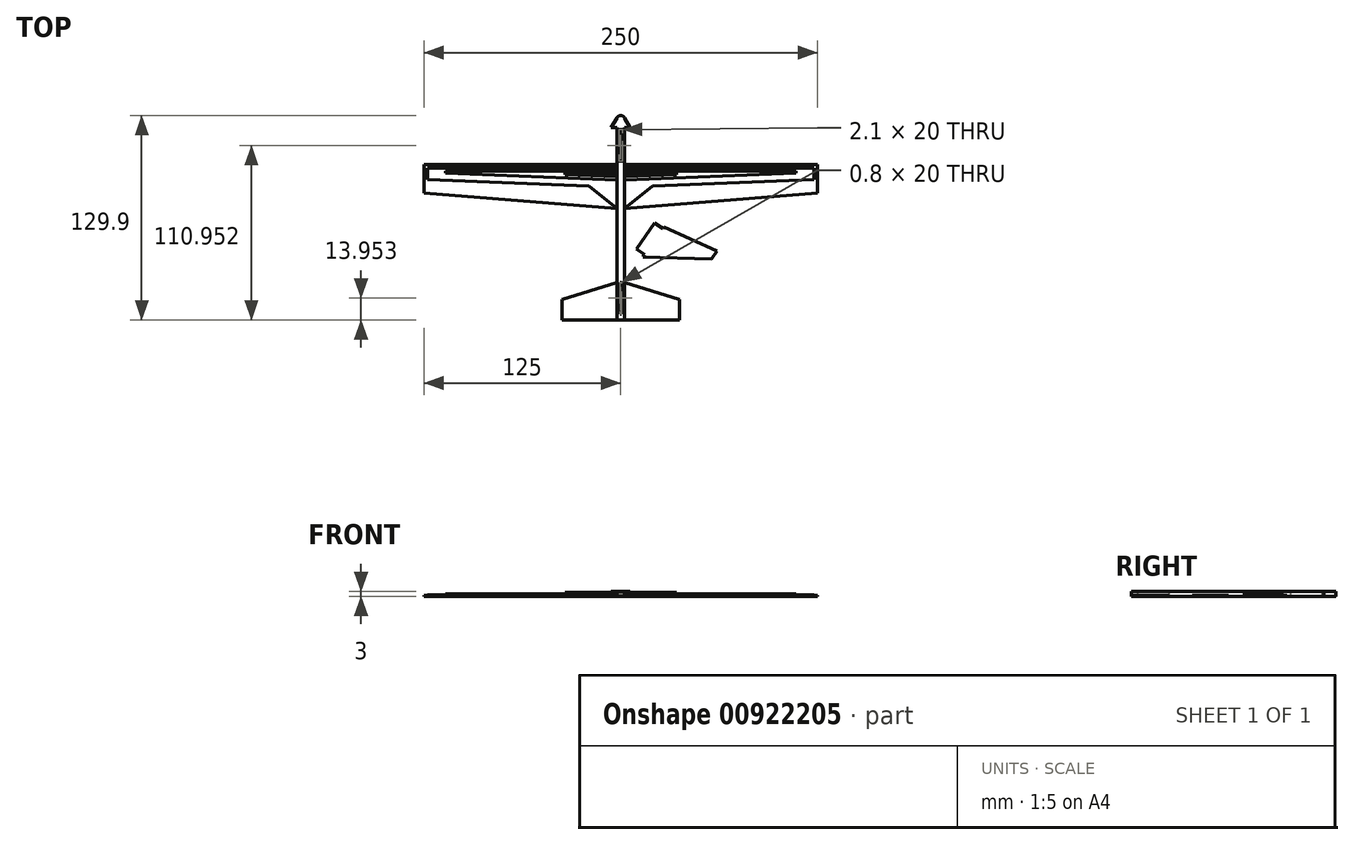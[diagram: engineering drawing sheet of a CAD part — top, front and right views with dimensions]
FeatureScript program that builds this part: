
annotation { "Feature Type Name" : "Feature", "Feature Type Description" : "" }
export const myFeature = defineFeature(function(context is Context, id is Id, definition is map)
    precondition{}
    {
        {
            var Q0;
            Q0=qCreatedBy(makeId("Top.planeOp"),FACE);
            var sketch = newSketch(context, id + "F0", { "sketchPlane" : qUnion([Q0])});
            skLineSegment(sketch, "E0", {"start": v(0, 139.35) * mm, "end": v(0, -90.2) * mm, "construction": true});
            skLineSegment(sketch, "E1", {"start": v(-125, 0) * mm, "end": v(0, 0) * mm, "construction": true});
            skLineSegment(sketch, "E2", {"start": v(0, 38.23) * mm, "end": v(-2.5, 38.23) * mm});
            skLineSegment(sketch, "E3", {"start": v(-2.5, 38.23) * mm, "end": v(-2.5, -90.2) * mm});
            skLineSegment(sketch, "E4", {"start": v(-2.5, -90.2) * mm, "end": v(0, -90.2) * mm});
            skLineSegment(sketch, "E5", {"start": v(-2.5, 8.48) * mm, "end": v(-125, 8.48) * mm});
            skLineSegment(sketch, "E6", {"start": v(-125, 8.48) * mm, "end": v(-125, 0) * mm});
            skLineSegment(sketch, "E7", {"start": v(-125, -9.54) * mm, "end": v(-2.5, -19.38) * mm});
            skLineSegment(sketch, "E8", {"start": v(-125, -9.54) * mm, "end": v(-125, 0) * mm});
            skLineSegment(sketch, "E9", {"start": v(-2.5, -66.26) * mm, "end": v(-37.22, -77.08) * mm});
            skLineSegment(sketch, "E10", {"start": v(-37.22, -77.08) * mm, "end": v(-37.22, -90.2) * mm});
            skLineSegment(sketch, "E11", {"start": v(-37.22, -90.2) * mm, "end": v(-2.5, -90.2) * mm});
            skLineSegment(sketch, "E12.MirrorCS", {"start": v(2.5, -90.2) * mm, "end": v(0, -90.2) * mm});
            skLineSegment(sketch, "E13.MirrorCS", {"start": v(37.22, -77.08) * mm, "end": v(37.22, -90.2) * mm});
            skLineSegment(sketch, "E14.MirrorCS", {"start": v(0, 38.23) * mm, "end": v(2.5, 38.23) * mm});
            skLineSegment(sketch, "E15.MirrorCS", {"start": v(37.22, -90.2) * mm, "end": v(2.5, -90.2) * mm});
            skLineSegment(sketch, "E16.MirrorCS", {"start": v(125, 0) * mm, "end": v(0, 0) * mm, "construction": true});
            skLineSegment(sketch, "E17.MirrorCS", {"start": v(2.5, 38.23) * mm, "end": v(2.5, -90.2) * mm});
            skLineSegment(sketch, "E18.MirrorCS", {"start": v(2.5, 8.48) * mm, "end": v(125, 8.48) * mm});
            skLineSegment(sketch, "E19.MirrorCS", {"start": v(125, 8.48) * mm, "end": v(125, 0) * mm});
            skLineSegment(sketch, "E20.MirrorCS", {"start": v(125, -9.54) * mm, "end": v(2.5, -19.38) * mm});
            skLineSegment(sketch, "E21.MirrorCS", {"start": v(2.5, -66.26) * mm, "end": v(37.22, -77.08) * mm});
            skLineSegment(sketch, "E22.MirrorCS", {"start": v(125, -9.54) * mm, "end": v(125, 0) * mm});
            skLineSegment(sketch, "E23", {"start": v(0, -66.26) * mm, "end": v(-0.4, -66.26) * mm});
            skLineSegment(sketch, "E24", {"start": v(-0.4, -66.26) * mm, "end": v(-0.4, -86.26) * mm});
            skLineSegment(sketch, "E25", {"start": v(-0.4, -86.26) * mm, "end": v(0, -86.26) * mm});
            skLineSegment(sketch, "E26.MirrorCS", {"start": v(0, -66.26) * mm, "end": v(0.4, -66.26) * mm});
            skLineSegment(sketch, "E27.MirrorCS", {"start": v(0.4, -66.26) * mm, "end": v(0.4, -86.26) * mm});
            skLineSegment(sketch, "E28.MirrorCS", {"start": v(0.4, -86.26) * mm, "end": v(0, -86.26) * mm});
            skLineSegment(sketch, "E29", {"start": v(14.14, -50.16) * mm, "end": v(57.48, -51.39) * mm});
            skLineSegment(sketch, "E30", {"start": v(57.48, -51.39) * mm, "end": v(61.1, -46.22) * mm});
            skLineSegment(sketch, "E31", {"start": v(61.1, -46.22) * mm, "end": v(27.57, -30.97) * mm});
            skLineSegment(sketch, "E32", {"start": v(27.57, -30.97) * mm, "end": v(26.7, -32.22) * mm});
            skLineSegment(sketch, "E33", {"start": v(26.7, -32.22) * mm, "end": v(21.46, -28.56) * mm});
            skLineSegment(sketch, "E34", {"start": v(9.98, -44.94) * mm, "end": v(15.22, -48.6) * mm});
            skLineSegment(sketch, "E35", {"start": v(15.22, -48.6) * mm, "end": v(14.14, -50.16) * mm});
            skLineSegment(sketch, "E36", {"start": v(9.98, -44.94) * mm, "end": v(21.46, -28.56) * mm});
            skLineSegment(sketch, "E37.0", {"start": v(27.57, -30.97) * mm, "end": v(14.14, -50.16) * mm, "construction": true});
            skLineSegment(sketch, "E38", {"start": v(0, 30.74) * mm, "end": v(-1.05, 30.74) * mm});
            skLineSegment(sketch, "E39", {"start": v(-1.05, 30.74) * mm, "end": v(-1.05, 10.74) * mm});
            skLineSegment(sketch, "E40", {"start": v(-1.05, 10.74) * mm, "end": v(0, 10.74) * mm});
            skLineSegment(sketch, "E41.MirrorCS", {"start": v(0, 30.74) * mm, "end": v(1.05, 30.74) * mm});
            skLineSegment(sketch, "E42.MirrorCS", {"start": v(1.05, 30.74) * mm, "end": v(1.05, 10.74) * mm});
            skLineSegment(sketch, "E43.MirrorCS", {"start": v(1.05, 10.74) * mm, "end": v(0, 10.74) * mm});
            skLineSegment(sketch, "E44", {"start": v(-2.5, 38.23) * mm, "end": v(-6.03, 31.96) * mm});
            skLineSegment(sketch, "E45", {"start": v(-6.03, 31.96) * mm, "end": v(-2.5, 31.96) * mm});
            skLineSegment(sketch, "E46.MirrorCS", {"start": v(2.5, 38.23) * mm, "end": v(6.03, 31.96) * mm});
            skLineSegment(sketch, "E47.MirrorCS", {"start": v(6.03, 31.96) * mm, "end": v(2.5, 31.96) * mm});
            skArc(sketch, "E48", {"start": v(2.5, 38.23) * mm, "mid": v(0, 39.69) * mm, "end": v(-2.5, 38.23) * mm});
            skSolve(sketch);
        }
        {
            var Q0;
            {var subQ1=sQuery(id+"F0.wireOp",EDGE,"E5");Q0=makeQuery(id+"F0.imprint","IMPRINT",FACE,{"disambiguationData":[TD([[makeQuery(id+"F0.imprint","IMPRINT",EDGE,{"derivedFrom":subQ1}),1.0]])]});}
            var Q1;
            {var subQ2=sQuery(id+"F0.wireOp",EDGE,"E9");Q1=makeQuery(id+"F0.imprint","IMPRINT",FACE,{"disambiguationData":[TD([[makeQuery(id+"F0.imprint","IMPRINT",EDGE,{"derivedFrom":subQ2}),1.0]])]});}
            var Q2;
            Q2=makeQuery(id+"F0.imprint","IMPRINT",FACE,{"disambiguationData":[TD([[makeQuery(id+"F0.imprint","IMPRINT",EDGE,{"derivedFrom":sQuery(id+"F0.wireOp",EDGE,"E13.MirrorCS")}),-1.0]])]});
            var Q3;
            {var subQ0=sQuery(id+"F0.wireOp",EDGE,"E18.MirrorCS");Q3=makeQuery(id+"F0.imprint","IMPRINT",FACE,{"disambiguationData":[TD([[makeQuery(id+"F0.imprint","IMPRINT",EDGE,{"derivedFrom":subQ0}),-1.0]])]});}
            var Q4;
            {var subQ7=sQuery(id+"F0.wireOp",EDGE,"E2");Q4=makeQuery(id+"F0.imprint","IMPRINT",FACE,{"disambiguationData":[TD([[makeQuery(id+"F0.imprint","IMPRINT",EDGE,{"derivedFrom":subQ7}),1.0]])]});}
            extrude(context, id + "F1", {"entities" : qUnion([Q0, Q1, Q2, Q3, Q4]), "depth" : 0.5 * mm, "offsetDistance" : 25 * mm});
        }
        {
            var Q0;
            {var subQ7=sQuery(id+"F0.wireOp",EDGE,"E2");Q0=makeQuery(id+"F0.imprint","IMPRINT",FACE,{"disambiguationData":[TD([[makeQuery(id+"F0.imprint","IMPRINT",EDGE,{"derivedFrom":subQ7}),1.0]])]});}
            var Q1;
            {var subQ0=sQuery(id+"F0.wireOp",EDGE,"fwCbbQgS-ba7Q-RRvG-tuf4-dKK3rzpyElhT");Q1=makeQuery(id+"F0.imprint","IMPRINT",FACE,{"disambiguationData":[TD([[makeQuery(id+"F0.imprint","IMPRINT",EDGE,{"derivedFrom":subQ0}),1.0]])]});}
            var Q2;
            {var subQ0=sQuery(id+"F0.wireOp",EDGE,"E44");Q2=makeQuery(id+"F0.imprint","IMPRINT",FACE,{"disambiguationData":[TD([[makeQuery(id+"F0.imprint","IMPRINT",EDGE,{"derivedFrom":subQ0}),1.0]])]});}
            var Q3;
            {var subQ0=sQuery(id+"F0.wireOp",EDGE,"E46.MirrorCS");Q3=makeQuery(id+"F0.imprint","IMPRINT",FACE,{"disambiguationData":[TD([[makeQuery(id+"F0.imprint","IMPRINT",EDGE,{"derivedFrom":subQ0}),-1.0]])]});}
            var Q4;
            Q4=makeQuery(id+"F0.imprint","IMPRINT",FACE,{"disambiguationData":[TD([[makeQuery(id+"F0.imprint","IMPRINT",EDGE,{"derivedFrom":sQuery(id+"F0.wireOp",EDGE,"E2")}),-1.0]])]});
            extrude(context, id + "F2", {"entities" : qUnion([Q0, Q1, Q2, Q3, Q4]), "operationType" : NewBodyOperationType.ADD, "depth" : 3 * mm, "offsetDistance" : 25 * mm});
        }
        {
            var Q0;
            {var subQ0=sQuery(id+"F0.wireOp",EDGE,"E8");var subQ1=sQuery(id+"F0.wireOp",EDGE,"E6");var subQ2=sQuery(id+"F0.wireOp",EDGE,"E3");var subQ3=sQuery(id+"F0.wireOp",EDGE,"E5");var subQ4=sQuery(id+"F0.wireOp",EDGE,"E7");var subQ5=sQuery(id+"F0.wireOp",EDGE,"E9");var subQ6=sQuery(id+"F0.wireOp",EDGE,"E2");Q0=makeQuery(id+"F2.boolean.opBoolean","SPLIT",FACE,{"disambiguationData":[TD([makeQuery(id+"F1.opExtrude","SWEPT_FACE",FACE,{"disambiguationData":[OSD([subQ3])]})])],"derivedFrom":makeQuery(id+"F1.opExtrude","CAP_FACE",FACE,{"disambiguationData":[OSD([subQ6,subQ2,sQuery(id+"F0.wireOp",EDGE,"E4"),subQ3,subQ1,subQ4,subQ0,subQ5,sQuery(id+"F0.wireOp",EDGE,"E10"),sQuery(id+"F0.wireOp",EDGE,"E11"),sQuery(id+"F0.wireOp",EDGE,"E12.MirrorCS"),sQuery(id+"F0.wireOp",EDGE,"E13.MirrorCS"),sQuery(id+"F0.wireOp",EDGE,"E14.MirrorCS"),sQuery(id+"F0.wireOp",EDGE,"E15.MirrorCS"),sQuery(id+"F0.wireOp",EDGE,"E17.MirrorCS"),sQuery(id+"F0.wireOp",EDGE,"E18.MirrorCS"),sQuery(id+"F0.wireOp",EDGE,"E19.MirrorCS"),sQuery(id+"F0.wireOp",EDGE,"E20.MirrorCS"),sQuery(id+"F0.wireOp",EDGE,"E21.MirrorCS"),sQuery(id+"F0.wireOp",EDGE,"E22.MirrorCS")])],"isStart":false})});}
            var sketch = newSketch(context, id + "F3", { "sketchPlane" : qUnion([Q0])});
            skLineSegment(sketch, "E49.0", {"start": v(0, 139.35) * mm, "end": v(0, -90.2) * mm});
            skLineSegment(sketch, "E50", {"start": v(0, 6.48) * mm, "end": v(-122.57, 6.48) * mm});
            skLineSegment(sketch, "E51", {"start": v(-122.57, 6.48) * mm, "end": v(-122.57, -0.97) * mm});
            skLineSegment(sketch, "E52", {"start": v(-122.57, -0.97) * mm, "end": v(0, -6.03) * mm});
            skLineSegment(sketch, "E53.MirrorCS", {"start": v(0, 6.48) * mm, "end": v(122.57, 6.48) * mm});
            skLineSegment(sketch, "E54.MirrorCS", {"start": v(122.57, 6.48) * mm, "end": v(122.57, -0.97) * mm});
            skLineSegment(sketch, "E55.MirrorCS", {"start": v(122.57, -0.97) * mm, "end": v(0, -6.03) * mm});
            skLineSegment(sketch, "E56", {"start": v(-20.21, -5.2) * mm, "end": v(-2.5, -19.38) * mm});
            skLineSegment(sketch, "E57", {"start": v(0, -19.38) * mm, "end": v(-2.5, -19.38) * mm});
            skLineSegment(sketch, "E58.MirrorCS", {"start": v(20.21, -5.2) * mm, "end": v(2.5, -19.38) * mm});
            skLineSegment(sketch, "E59.MirrorCS", {"start": v(0, -19.38) * mm, "end": v(2.5, -19.38) * mm});
            skSolve(sketch);
        }
        {
            var Q0;
            {var subQ0=sQuery(id+"F3.wireOp",EDGE,"E51");Q0=makeQuery(id+"F3.imprint","IMPRINT",FACE,{"disambiguationData":[TD([[makeQuery(id+"F3.imprint","IMPRINT",EDGE,{"derivedFrom":subQ0}),1.0]])]});}
            var Q1;
            {var subQ0=sQuery(id+"F3.wireOp",EDGE,"E53.MirrorCS");Q1=makeQuery(id+"F3.imprint","IMPRINT",FACE,{"disambiguationData":[TD([[makeQuery(id+"F3.imprint","IMPRINT",EDGE,{"derivedFrom":subQ0}),-1.0]])]});}
            var Q2;
            {var subQ0=sQuery(id+"F3.wireOp",EDGE,"E56");Q2=makeQuery(id+"F3.imprint","IMPRINT",FACE,{"disambiguationData":[TD([[makeQuery(id+"F3.imprint","IMPRINT",EDGE,{"derivedFrom":subQ0}),1.0]])]});}
            var Q3;
            {var subQ4=sQuery(id+"F3.wireOp",EDGE,"E58.MirrorCS");Q3=makeQuery(id+"F3.imprint","IMPRINT",FACE,{"disambiguationData":[TD([[makeQuery(id+"F3.imprint","IMPRINT",EDGE,{"derivedFrom":subQ4}),-1.0]])]});}
            extrude(context, id + "F4", {"entities" : qUnion([Q0, Q1, Q2, Q3]), "operationType" : NewBodyOperationType.ADD, "depth" : 0.5 * mm, "offsetDistance" : 25 * mm});
        }
        {
            var Q0;
            Q0=makeQuery(id+"F0.imprint","IMPRINT",FACE,{"disambiguationData":[TD([[makeQuery(id+"F0.imprint","IMPRINT",EDGE,{"derivedFrom":sQuery(id+"F0.wireOp",EDGE,"E29")}),1.0]])]});
            extrude(context, id + "F5", {"entities" : qUnion([Q0]), "depth" : 0.5 * mm, "offsetDistance" : 25 * mm});
        }
        {
            var Q0;
            Q0=makeQuery(id+"F4.opExtrude","CAP_FACE",FACE,{"disambiguationData":[OSD([sQuery(id+"F0.wireOp",EDGE,"E2"),sQuery(id+"F0.wireOp",EDGE,"E3"),sQuery(id+"F0.wireOp",EDGE,"E4"),sQuery(id+"F0.wireOp",EDGE,"E5"),sQuery(id+"F0.wireOp",EDGE,"E6"),sQuery(id+"F0.wireOp",EDGE,"E7"),sQuery(id+"F0.wireOp",EDGE,"E8"),sQuery(id+"F0.wireOp",EDGE,"E9"),sQuery(id+"F0.wireOp",EDGE,"E10"),sQuery(id+"F0.wireOp",EDGE,"E11"),sQuery(id+"F0.wireOp",EDGE,"E12.MirrorCS"),sQuery(id+"F0.wireOp",EDGE,"E13.MirrorCS"),sQuery(id+"F0.wireOp",EDGE,"E14.MirrorCS"),sQuery(id+"F0.wireOp",EDGE,"E15.MirrorCS"),sQuery(id+"F0.wireOp",EDGE,"E17.MirrorCS"),sQuery(id+"F0.wireOp",EDGE,"E18.MirrorCS"),sQuery(id+"F0.wireOp",EDGE,"E19.MirrorCS"),sQuery(id+"F0.wireOp",EDGE,"E20.MirrorCS"),sQuery(id+"F0.wireOp",EDGE,"E21.MirrorCS"),sQuery(id+"F0.wireOp",EDGE,"E22.MirrorCS"),sQuery(id+"F0.wireOp",EDGE,"E23"),sQuery(id+"F0.wireOp",EDGE,"E24"),sQuery(id+"F0.wireOp",EDGE,"E25"),sQuery(id+"F0.wireOp",EDGE,"E26.MirrorCS"),sQuery(id+"F0.wireOp",EDGE,"E27.MirrorCS"),sQuery(id+"F0.wireOp",EDGE,"E28.MirrorCS"),sQuery(id+"F3.wireOp",EDGE,"E50"),sQuery(id+"F3.wireOp",EDGE,"E51"),sQuery(id+"F3.wireOp",EDGE,"E52")])],"isStart":false});
            var sketch = newSketch(context, id + "F6", { "sketchPlane" : qUnion([Q0])});
            skLineSegment(sketch, "E60", {"start": v(0, 4.48) * mm, "end": v(-111.3, 4.48) * mm});
            skLineSegment(sketch, "E61", {"start": v(-111.3, 4.48) * mm, "end": v(-111.3, 3.13) * mm});
            skLineSegment(sketch, "E62", {"start": v(-111.3, 3.13) * mm, "end": v(0, -1.47) * mm});
            skLineSegment(sketch, "E63.MirrorCS", {"start": v(0, 4.48) * mm, "end": v(111.3, 4.48) * mm});
            skLineSegment(sketch, "E64.MirrorCS", {"start": v(111.3, 4.48) * mm, "end": v(111.3, 3.13) * mm});
            skLineSegment(sketch, "E65.MirrorCS", {"start": v(111.3, 3.13) * mm, "end": v(0, -1.47) * mm});
            skSolve(sketch);
        }
        {
            var Q0;
            Q0 = qSketchRegion(id + "F6", true);
            extrude(context, id + "F7", {"entities" : qUnion([Q0]), "operationType" : NewBodyOperationType.ADD, "depth" : 0.5 * mm, "offsetDistance" : 25 * mm});
        }
        {
            var Q0;
            {var subQ0=sQuery(id+"F6.wireOp",EDGE,"E63.MirrorCS");var subQ1=sQuery(id+"F6.wireOp",EDGE,"E60");var subQ2=sQuery(id+"F0.wireOp",EDGE,"E3");var subQ4=sQuery(id+"F6.wireOp",EDGE,"E61");var subQ5=sQuery(id+"F6.wireOp",EDGE,"E62");Q0=makeQuery(id+"F7.boolean.opBoolean","SPLIT",FACE,{"disambiguationData":[TD([makeQuery(id+"F2.opExtrude","SWEPT_FACE",FACE,{"disambiguationData":[OSD([subQ2])]})])],"derivedFrom":makeQuery(id+"F7.opExtrude","CAP_FACE",FACE,{"disambiguationData":[OSD([subQ1,subQ4,subQ5,subQ0,sQuery(id+"F6.wireOp",EDGE,"E64.MirrorCS"),sQuery(id+"F6.wireOp",EDGE,"E65.MirrorCS")])],"isStart":false})});}
            var sketch = newSketch(context, id + "F8", { "sketchPlane" : qUnion([Q0])});
            skLineSegment(sketch, "E66", {"start": v(0, 3.1) * mm, "end": v(-35.45, 3.1) * mm});
            skLineSegment(sketch, "E67", {"start": v(-35.45, 3.1) * mm, "end": v(-35.45, 2.15) * mm});
            skLineSegment(sketch, "E68", {"start": v(-35.45, 2.15) * mm, "end": v(0, 1) * mm});
            skLineSegment(sketch, "E69.MirrorCS", {"start": v(0, 3.1) * mm, "end": v(35.45, 3.1) * mm});
            skLineSegment(sketch, "E70.MirrorCS", {"start": v(35.45, 3.1) * mm, "end": v(35.45, 2.15) * mm});
            skLineSegment(sketch, "E71.MirrorCS", {"start": v(35.45, 2.15) * mm, "end": v(0, 1) * mm});
            skSolve(sketch);
        }
        {
            var Q0;
            {var subQ0=sQuery(id+"F8.wireOp",EDGE,"E67");Q0=makeQuery(id+"F8.imprint","IMPRINT",FACE,{"disambiguationData":[TD([[makeQuery(id+"F8.imprint","IMPRINT",EDGE,{"derivedFrom":subQ0}),1.0]])]});}
            var Q1;
            {var subQ6=sQuery(id+"F8.wireOp",EDGE,"E69.MirrorCS");Q1=makeQuery(id+"F8.imprint","IMPRINT",FACE,{"disambiguationData":[TD([[makeQuery(id+"F8.imprint","IMPRINT",EDGE,{"derivedFrom":subQ6}),-1.0]])]});}
            extrude(context, id + "F9", {"entities" : qUnion([Q0, Q1]), "operationType" : NewBodyOperationType.ADD, "depth" : 1 * mm, "offsetDistance" : 25 * mm});
        }
    });
